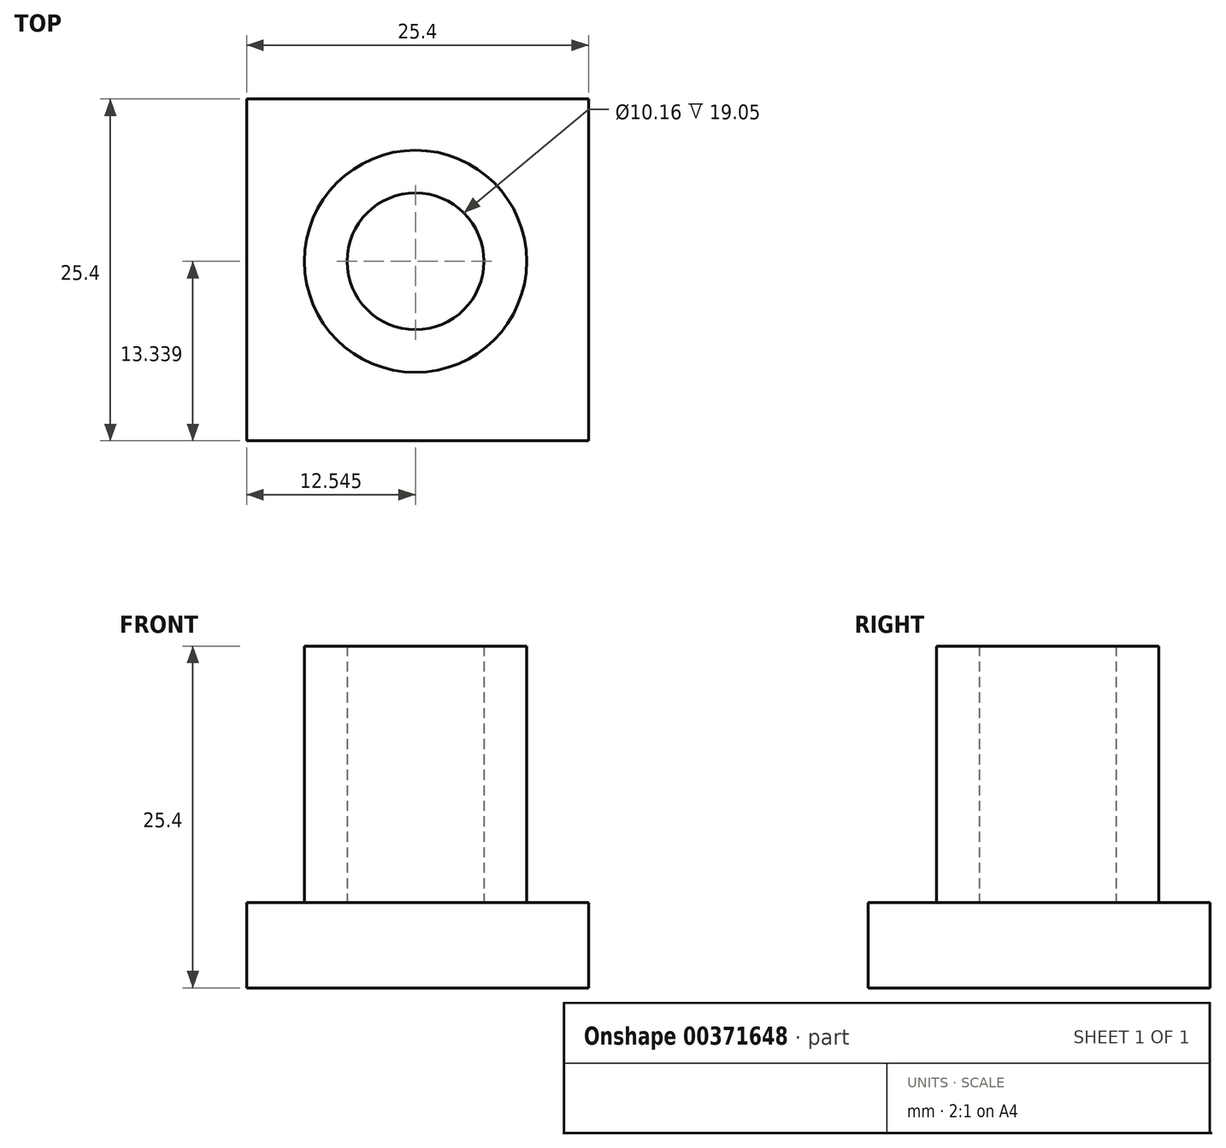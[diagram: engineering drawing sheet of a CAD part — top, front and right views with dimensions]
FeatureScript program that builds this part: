
annotation { "Feature Type Name" : "Feature", "Feature Type Description" : "" }
export const myFeature = defineFeature(function(context is Context, id is Id, definition is map)
    precondition{}
    {
        {
            var Q0;
            Q0=qCreatedBy(makeId("Top.planeOp"),FACE);
            var sketch = newSketch(context, id + "F0", { "sketchPlane" : qUnion([Q0])});
            skLineSegment(sketch, "E0.bottom", {"start": v(-38.68, 50.08) * mm, "end": v(-13.28, 50.08) * mm});
            skLineSegment(sketch, "E0.top", {"start": v(-38.68, 24.68) * mm, "end": v(-13.28, 24.68) * mm});
            skLineSegment(sketch, "E0.left", {"start": v(-38.68, 50.08) * mm, "end": v(-38.68, 24.68) * mm});
            skLineSegment(sketch, "E0.right", {"start": v(-13.28, 50.08) * mm, "end": v(-13.28, 24.68) * mm});
            skSolve(sketch);
        }
        {
            var Q0;
            Q0 = qSketchRegion(id + "F0", true);
            extrude(context, id + "F1", {"entities" : qUnion([Q0]), "depth" : 6.35 * mm});
        }
        {
            var Q0;
            Q0=qCreatedBy(makeId("Top.planeOp"),FACE);
            var sketch = newSketch(context, id + "F2", { "sketchPlane" : qUnion([Q0])});
            skCircle(sketch, "E1", {"center": v(-26.13, 38.02) * mm, "radius": 8.26 * mm});
            skCircle(sketch, "E2", {"center": v(-26.13, 38.02) * mm, "radius": 5.08 * mm});
            skSolve(sketch);
        }
        {
            var Q0;
            Q0 = qSketchRegion(id + "F2", true);
            extrude(context, id + "F3", {"entities" : qUnion([Q0]), "operationType" : NewBodyOperationType.ADD, "depth" : 25.4 * mm});
        }
    });
